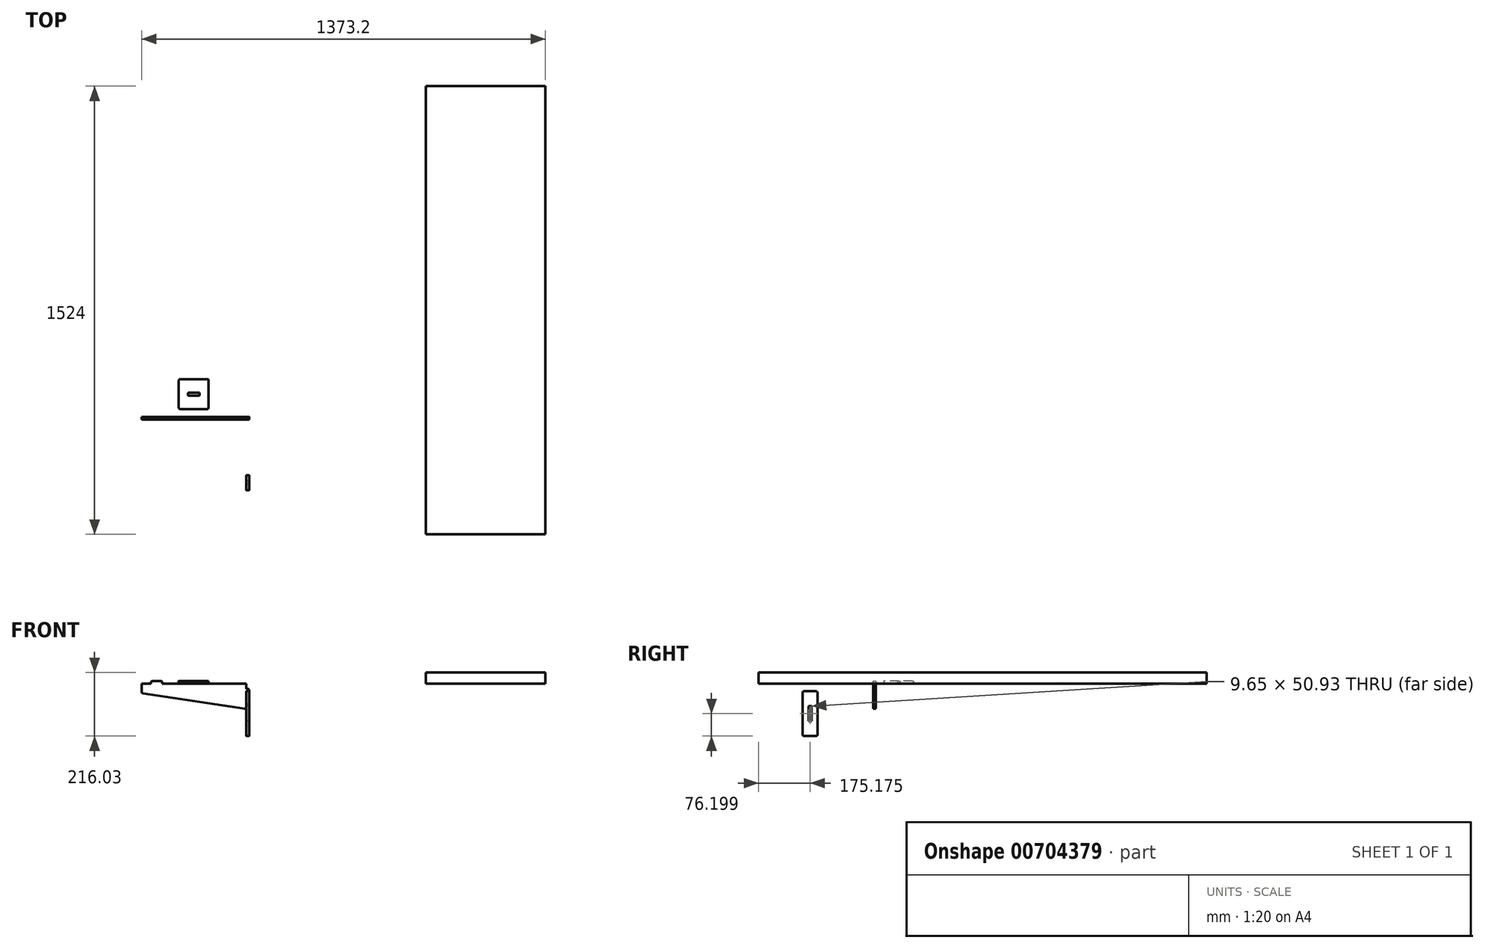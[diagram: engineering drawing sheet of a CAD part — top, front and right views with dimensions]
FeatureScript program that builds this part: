
annotation { "Feature Type Name" : "Feature", "Feature Type Description" : "" }
export const myFeature = defineFeature(function(context is Context, id is Id, definition is map)
    precondition{}
    {
        {
            var Q0;
            Q0=qCreatedBy(makeId("Front.planeOp"),FACE);
            var sketch = newSketch(context, id + "F0", { "sketchPlane" : qUnion([Q0])});
            skLineSegment(sketch, "E0", {"start": v(0, 0) * mm, "end": v(-355.6, 0) * mm});
            skLineSegment(sketch, "E1", {"start": v(-355.6, 0) * mm, "end": v(-355.6, -31.75) * mm});
            skLineSegment(sketch, "E2", {"start": v(-355.6, -31.75) * mm, "end": v(0, -85.73) * mm});
            skLineSegment(sketch, "E3", {"start": v(0, -85.73) * mm, "end": v(0, 0) * mm});
            skPoint(sketch, "E4", {"position": v(-323.85, 0) * mm});
            skLineSegment(sketch, "E5.top", {"start": v(-323.85, 9.52) * mm, "end": v(-285.75, 9.52) * mm});
            skLineSegment(sketch, "E5.left", {"start": v(-323.85, 0) * mm, "end": v(-323.85, 9.52) * mm});
            skLineSegment(sketch, "E5.right", {"start": v(-285.75, 0) * mm, "end": v(-285.75, 9.52) * mm});
            skPoint(sketch, "E6", {"position": v(0, -17.46) * mm});
            skLineSegment(sketch, "E7.bottom", {"start": v(0, -17.46) * mm, "end": v(9.52, -17.46) * mm});
            skLineSegment(sketch, "E7.top", {"start": v(0, -68.26) * mm, "end": v(9.53, -68.26) * mm});
            skLineSegment(sketch, "E7.left", {"start": v(0, -17.46) * mm, "end": v(0, -68.26) * mm});
            skLineSegment(sketch, "E7.right", {"start": v(9.52, -17.46) * mm, "end": v(9.53, -68.26) * mm});
            skSolve(sketch);
        }
        {
            var Q0;
            {var subQ0=sQuery(id+"F0.wireOp",EDGE,"E1");Q0=makeQuery(id+"F0.imprint","IMPRINT",FACE,{"disambiguationData":[TD([[makeQuery(id+"F0.imprint","IMPRINT",EDGE,{"derivedFrom":subQ0}),1.0]])]});}
            var Q1;
            Q1=makeQuery(id+"F0.imprint","IMPRINT",FACE,{"disambiguationData":[TD([[makeQuery(id+"F0.imprint","IMPRINT",EDGE,{"derivedFrom":sQuery(id+"F0.wireOp",EDGE,"E5.top")}),-1.0]])]});
            var Q2;
            Q2=makeQuery(id+"F0.imprint","IMPRINT",FACE,{"disambiguationData":[TD([[makeQuery(id+"F0.imprint","IMPRINT",EDGE,{"derivedFrom":sQuery(id+"F0.wireOp",EDGE,"E7.bottom")}),-1.0]])]});
            extrude(context, id + "F1", {"entities" : qUnion([Q0, Q1, Q2]), "depth" : 9.52 * mm, "offsetDistance" : 25.4 * mm});
        }
        {
            var Q0;
            Q0=makeQuery(id+"F1.opExtrude","SWEPT_EDGE",EDGE,{"disambiguationData":[OSD([sQuery(id+"F0.wireOp",EDGE,"E1"),sQuery(id+"F0.wireOp",EDGE,"E2")])]});
            var Q1;
            Q1=makeQuery(id+"F1.opExtrude","SWEPT_EDGE",EDGE,{"disambiguationData":[OSD([sQuery(id+"F0.wireOp",EDGE,"E5.top"),sQuery(id+"F0.wireOp",EDGE,"E5.left")])]});
            var Q2;
            Q2=makeQuery(id+"F1.opExtrude","SWEPT_EDGE",EDGE,{"disambiguationData":[OSD([sQuery(id+"F0.wireOp",EDGE,"E5.top"),sQuery(id+"F0.wireOp",EDGE,"E5.right")])]});
            var Q3;
            Q3=makeQuery(id+"F1.opExtrude","SWEPT_EDGE",EDGE,{"disambiguationData":[OSD([sQuery(id+"F0.wireOp",EDGE,"E2"),sQuery(id+"F0.wireOp",EDGE,"E3")])]});
            var Q4;
            Q4=makeQuery(id+"F1.opExtrude","SWEPT_EDGE",EDGE,{"disambiguationData":[OSD([sQuery(id+"F0.wireOp",EDGE,"E7.bottom"),sQuery(id+"F0.wireOp",EDGE,"E7.right")])]});
            var Q5;
            Q5=makeQuery(id+"F1.opExtrude","SWEPT_EDGE",EDGE,{"disambiguationData":[OSD([sQuery(id+"F0.wireOp",EDGE,"E7.top"),sQuery(id+"F0.wireOp",EDGE,"E7.right")])]});
            fillet(context, id + "F2", {"entities" : qUnion([Q0, Q1, Q2, Q3, Q4, Q5]), "radius" : 4.76 * mm, "tangentPropagation" : true, "allowEdgeOverflow" : false});
        }
        {
            var Q0;
            Q0=qCreatedBy(makeId("Top.planeOp"),FACE);
            var sketch = newSketch(context, id + "F3", { "sketchPlane" : qUnion([Q0])});
            skLineSegment(sketch, "E8.bottom", {"start": v(-229.51, 128.47) * mm, "end": v(-127.91, 128.47) * mm});
            skLineSegment(sketch, "E8.top", {"start": v(-229.51, 26.87) * mm, "end": v(-127.91, 26.87) * mm});
            skLineSegment(sketch, "E8.left", {"start": v(-229.51, 128.47) * mm, "end": v(-229.51, 26.87) * mm});
            skLineSegment(sketch, "E8.right", {"start": v(-127.91, 128.47) * mm, "end": v(-127.91, 26.87) * mm});
            skPoint(sketch, "E9", {"position": v(-178.71, 77.67) * mm});
            skLineSegment(sketch, "E10.bottom", {"start": v(-159.03, 72.84) * mm, "end": v(-198.4, 72.84) * mm});
            skLineSegment(sketch, "E10.top", {"start": v(-159.03, 82.5) * mm, "end": v(-198.4, 82.5) * mm});
            skLineSegment(sketch, "E10.left", {"start": v(-159.03, 72.84) * mm, "end": v(-159.03, 82.5) * mm});
            skLineSegment(sketch, "E10.right", {"start": v(-198.4, 72.84) * mm, "end": v(-198.4, 82.5) * mm});
            skSolve(sketch);
        }
        {
            var Q0;
            Q0=makeQuery(id+"F3.imprint","IMPRINT",FACE,{"disambiguationData":[TD([[makeQuery(id+"F3.imprint","IMPRINT",EDGE,{"derivedFrom":sQuery(id+"F3.wireOp",EDGE,"E8.bottom")}),-1.0]])]});
            extrude(context, id + "F4", {"entities" : qUnion([Q0]), "depth" : 9.52 * mm, "offsetDistance" : 25.4 * mm});
        }
        {
            var Q0;
            Q0=makeQuery(id+"F4.opExtrude","SWEPT_EDGE",EDGE,{"disambiguationData":[OSD([sQuery(id+"F3.wireOp",EDGE,"E8.top"),sQuery(id+"F3.wireOp",EDGE,"E8.left")])]});
            var Q1;
            Q1=makeQuery(id+"F4.opExtrude","SWEPT_EDGE",EDGE,{"disambiguationData":[OSD([sQuery(id+"F3.wireOp",EDGE,"E8.bottom"),sQuery(id+"F3.wireOp",EDGE,"E8.left")])]});
            var Q2;
            Q2=makeQuery(id+"F4.opExtrude","SWEPT_EDGE",EDGE,{"disambiguationData":[OSD([sQuery(id+"F3.wireOp",EDGE,"E8.top"),sQuery(id+"F3.wireOp",EDGE,"E8.right")])]});
            var Q3;
            Q3=makeQuery(id+"F4.opExtrude","SWEPT_EDGE",EDGE,{"disambiguationData":[OSD([sQuery(id+"F3.wireOp",EDGE,"E8.bottom"),sQuery(id+"F3.wireOp",EDGE,"E8.right")])]});
            fillet(context, id + "F5", {"entities" : qUnion([Q0, Q1, Q2, Q3]), "radius" : 4.76 * mm, "tangentPropagation" : true, "allowEdgeOverflow" : false});
        }
        {
            var Q0;
            Q0=qCreatedBy(makeId("Top.planeOp"),FACE);
            var sketch = newSketch(context, id + "F6", { "sketchPlane" : qUnion([Q0])});
            skLineSegment(sketch, "E11.bottom", {"start": v(611.2, 1124.95) * mm, "end": v(1017.6, 1124.95) * mm});
            skLineSegment(sketch, "E11.top", {"start": v(611.2, -399.05) * mm, "end": v(1017.6, -399.05) * mm});
            skLineSegment(sketch, "E11.left", {"start": v(611.2, 1124.95) * mm, "end": v(611.2, -399.05) * mm});
            skLineSegment(sketch, "E11.right", {"start": v(1017.6, 1124.95) * mm, "end": v(1017.6, -399.05) * mm});
            skSolve(sketch);
        }
        {
            var Q0;
            Q0=makeQuery(id+"F6.imprint","IMPRINT",FACE,{"disambiguationData":[TD([[makeQuery(id+"F6.imprint","IMPRINT",EDGE,{"derivedFrom":sQuery(id+"F6.wireOp",EDGE,"E11.bottom")}),-1.0]])]});
            extrude(context, id + "F7", {"entities" : qUnion([Q0]), "depth" : 38.1 * mm, "offsetDistance" : 25.4 * mm});
        }
        {
            var Q0;
            Q0=qCreatedBy(makeId("Right.planeOp"),FACE);
            var sketch = newSketch(context, id + "F8", { "sketchPlane" : qUnion([Q0])});
            skLineSegment(sketch, "E12.bottom", {"start": v(-249.27, -25.53) * mm, "end": v(-198.47, -25.53) * mm});
            skLineSegment(sketch, "E12.top", {"start": v(-249.27, -177.93) * mm, "end": v(-198.47, -177.93) * mm});
            skLineSegment(sketch, "E12.left", {"start": v(-249.27, -25.53) * mm, "end": v(-249.27, -177.93) * mm});
            skLineSegment(sketch, "E12.right", {"start": v(-198.47, -25.53) * mm, "end": v(-198.47, -177.93) * mm});
            skPoint(sketch, "E13", {"position": v(-223.87, -101.73) * mm});
            skPoint(sketch, "E13.positionSnap0", {"position": v(-198.47, -101.73) * mm});
            skLineSegment(sketch, "E14.bottom", {"start": v(-228.7, -76.27) * mm, "end": v(-219.05, -76.27) * mm});
            skLineSegment(sketch, "E14.top", {"start": v(-228.7, -127.2) * mm, "end": v(-219.05, -127.2) * mm});
            skLineSegment(sketch, "E14.left", {"start": v(-228.7, -76.27) * mm, "end": v(-228.7, -127.2) * mm});
            skLineSegment(sketch, "E14.right", {"start": v(-219.05, -76.27) * mm, "end": v(-219.05, -127.2) * mm});
            skSolve(sketch);
        }
        {
            var Q0;
            Q0=makeQuery(id+"F8.imprint","IMPRINT",FACE,{"disambiguationData":[TD([[makeQuery(id+"F8.imprint","IMPRINT",EDGE,{"derivedFrom":sQuery(id+"F8.wireOp",EDGE,"E12.bottom")}),-1.0]])]});
            extrude(context, id + "F9", {"entities" : qUnion([Q0]), "depth" : 9.52 * mm, "offsetDistance" : 25.4 * mm});
        }
        {
            var Q0;
            Q0=makeQuery(id+"F9.opExtrude","SWEPT_EDGE",EDGE,{"disambiguationData":[OSD([sQuery(id+"F8.wireOp",EDGE,"E12.bottom"),sQuery(id+"F8.wireOp",EDGE,"E12.left")])]});
            var Q1;
            Q1=makeQuery(id+"F9.opExtrude","SWEPT_EDGE",EDGE,{"disambiguationData":[OSD([sQuery(id+"F8.wireOp",EDGE,"E12.top"),sQuery(id+"F8.wireOp",EDGE,"E12.left")])]});
            var Q2;
            Q2=makeQuery(id+"F9.opExtrude","SWEPT_EDGE",EDGE,{"disambiguationData":[OSD([sQuery(id+"F8.wireOp",EDGE,"E12.top"),sQuery(id+"F8.wireOp",EDGE,"E12.right")])]});
            var Q3;
            Q3=makeQuery(id+"F9.opExtrude","SWEPT_EDGE",EDGE,{"disambiguationData":[OSD([sQuery(id+"F8.wireOp",EDGE,"E12.bottom"),sQuery(id+"F8.wireOp",EDGE,"E12.right")])]});
            fillet(context, id + "F10", {"entities" : qUnion([Q0, Q1, Q2, Q3]), "radius" : 5.08 * mm, "tangentPropagation" : true, "allowEdgeOverflow" : false});
        }
    });
